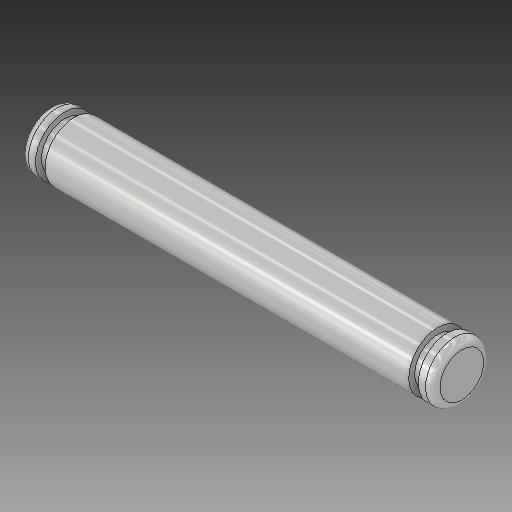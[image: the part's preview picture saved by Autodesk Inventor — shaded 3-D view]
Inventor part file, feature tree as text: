
AUTODESK INVENTOR PART (.ipt)
format: ipt  version: 2018 (Build 220112000, 112)  size: 150,528 bytes
history: native  units: mm
features: revolve x1, sketch x1
ambient origin geometry x8: Origin, YZ Plane, XZ Plane, XY Plane, X Axis, Y Axis, Z Axis, Center Point
bodies: Solid1 (feature_tree)
feature tree (2):
  revolve  "Revolution1"  [1 undecoded]
  sketch  "Sketch1"  dims[d0=25.0mm d1=0.65mm d2=1.0mm d3=2.0mm d4=1.6mm d5=1.6mm d6=0.5mm d7=1.0mm d8=0.5mm d9=90.0deg]
note: 1 required parameter value undecoded (feature->parameter linkage not recoverable at this tier; creation-order binding heuristic only, values carry confidence <= 0.55)
